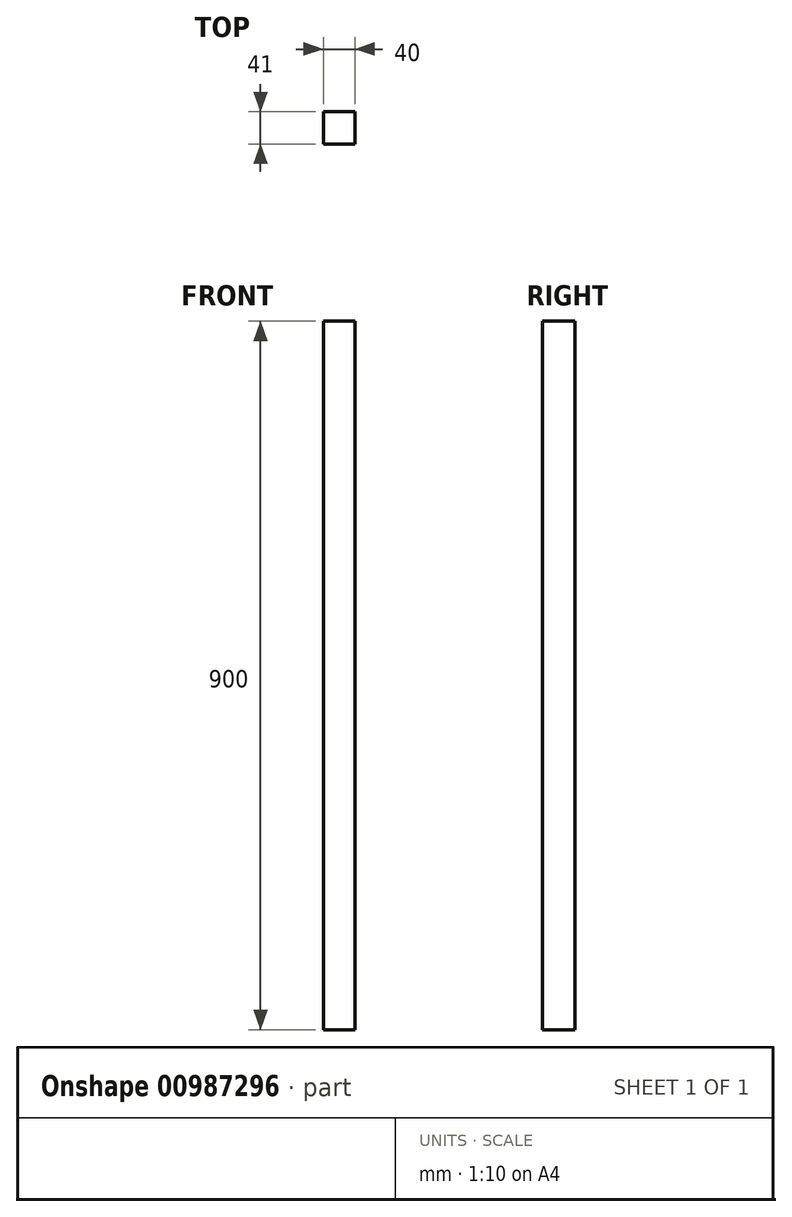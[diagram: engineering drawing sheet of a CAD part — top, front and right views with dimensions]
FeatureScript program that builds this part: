
annotation { "Feature Type Name" : "Feature", "Feature Type Description" : "" }
export const myFeature = defineFeature(function(context is Context, id is Id, definition is map)
    precondition{}
    {
        {
            var Q0;
            Q0=qCreatedBy(makeId("Front.planeOp"),FACE);
            var sketch = newSketch(context, id + "F0", { "sketchPlane" : qUnion([Q0])});
            skLineSegment(sketch, "E0.bottom", {"start": v(-21.43, 0) * mm, "end": v(18.57, 0) * mm});
            skLineSegment(sketch, "E0.top", {"start": v(-21.43, 900) * mm, "end": v(18.57, 900) * mm});
            skLineSegment(sketch, "E0.left", {"start": v(-21.43, 0) * mm, "end": v(-21.43, 900) * mm});
            skLineSegment(sketch, "E0.right", {"start": v(18.57, 0) * mm, "end": v(18.57, 900) * mm});
            skSolve(sketch);
        }
        {
            var Q0;
            Q0=makeQuery(id+"F0.imprint","IMPRINT",FACE,{"disambiguationData":[TD([[makeQuery(id+"F0.imprint","IMPRINT",EDGE,{"derivedFrom":sQuery(id+"F0.wireOp",EDGE,"E0.bottom")}),1.0]])]});
            extrude(context, id + "F1", {"entities" : qUnion([Q0]), "depth" : 41 * mm, "offsetDistance" : 25 * mm});
        }
    });
